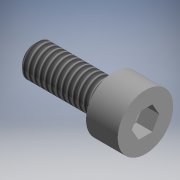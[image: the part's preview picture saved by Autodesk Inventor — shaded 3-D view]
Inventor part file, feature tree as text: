
AUTODESK INVENTOR PART (.ipt)
format: ipt  version: 2017.3 (Build 213256000, 256)  size: 123,392 bytes
history: native  units: mm (DEFAULTED — no unit token found)
features: other x14, sketch x3, revolve x1, thread x1, hole x1, extrude x1
ambient origin geometry x8: Origin, YZ Plane, XZ Plane, XY Plane, X Axis, Y Axis, Z Axis, Center Point
bodies: Solid1 (feature_tree)
feature tree (21):
  revolve  "Revolution1"  [1 undecoded]
  thread  "Thread1"  [1 undecoded]
  hole  "Hole1"  [1 undecoded]
  extrude  "Extrusion1"  [1 undecoded]
  other  "bolt_to_nut_XY"
  other  "bolt_to_nut_YZ"
  other  "bolt_to_nut_ZX"
  other  "bolt_to_nut_X"
  other  "bolt_to_nut_Y"
  other  "bolt_to_nut_Z"
  other  "bolt_to_nut_Center"
  other  "screw1_XY"
  other  "screw1_YZ"
  other  "screw1_ZX"
  other  "screw1_X"
  other  "screw1_Y"
  other  "screw1_Z"
  other  "screw1_Center"
  sketch  "Sketch_1"  dims[d0=360.0deg d1=8.5705mm d2=0.0mm]
  sketch  "Sketch2"  dims[d3=3.0mm d4=6.0mm d5=4.0mm d6=2.0mm d7=90.0deg d8=2.0mm d9=150.0deg d10=2.0mm d11=0.0mm]
  sketch  "Sketch_3"  dims[d12=0.0mm d13=0.0mm]
note: 4 required parameter values undecoded (feature->parameter linkage not recoverable at this tier; creation-order binding heuristic only, values carry confidence <= 0.55)